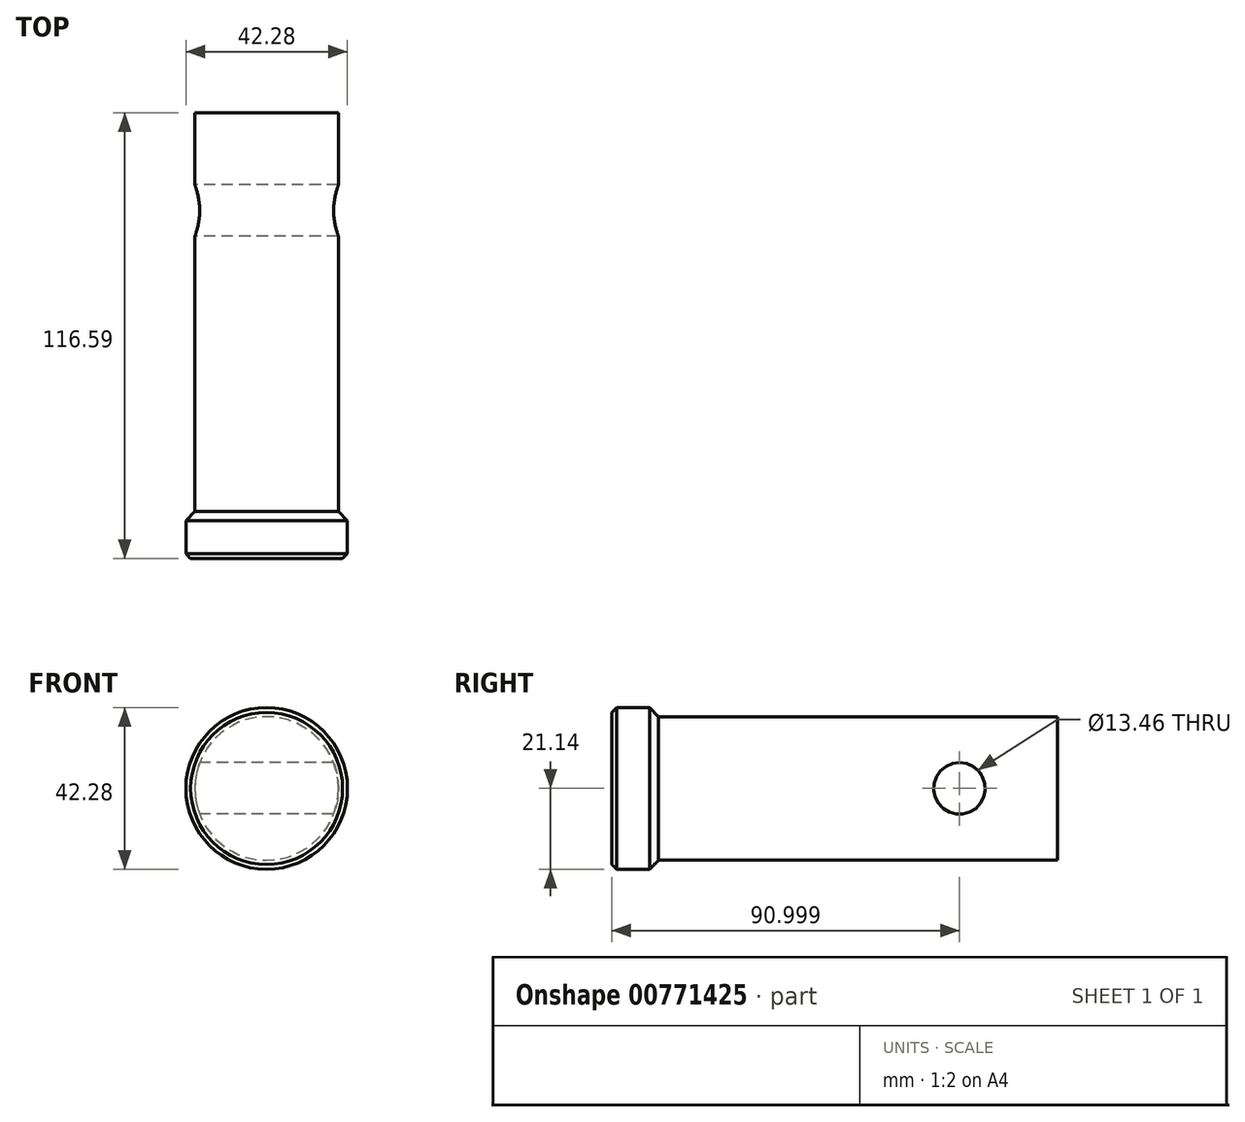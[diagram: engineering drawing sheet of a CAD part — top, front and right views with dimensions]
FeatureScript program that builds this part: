
annotation { "Feature Type Name" : "Feature", "Feature Type Description" : "" }
export const myFeature = defineFeature(function(context is Context, id is Id, definition is map)
    precondition{}
    {
        {
            var Q0;
            Q0=qCreatedBy(makeId("Front.planeOp"),FACE);
            var sketch = newSketch(context, id + "F0", { "sketchPlane" : qUnion([Q0])});
            skCircle(sketch, "E0", {"center": v(0, 0) * mm, "radius": 18.77 * mm});
            skSolve(sketch);
        }
        {
            var Q0;
            Q0 = qSketchRegion(id + "F0", true);
            extrude(context, id + "F1", {"entities" : qUnion([Q0]), "oppositeDirection" : true, "depth" : 101.6 * mm, "offsetDistance" : 25.4 * mm});
        }
        {
            var Q0;
            Q0=qCreatedBy(makeId("Front.planeOp"),FACE);
            var sketch = newSketch(context, id + "F2", { "sketchPlane" : qUnion([Q0])});
            skCircle(sketch, "E1", {"center": v(0, 0) * mm, "radius": 21.14 * mm});
            skSolve(sketch);
        }
        {
            var Q0;
            Q0 = qSketchRegion(id + "F2", true);
            extrude(context, id + "F3", {"entities" : qUnion([Q0]), "operationType" : NewBodyOperationType.ADD, "depth" : 15 * mm, "offsetDistance" : 25.4 * mm});
        }
        {
            var Q0;
            Q0=makeQuery(id+"F3.opExtrude","CAP_EDGE",EDGE,{"disambiguationData":[OSD([sQuery(id+"F2.wireOp",EDGE,"E1")])],"isStart":true});
            chamfer(context, id + "F4", {"entities" : qUnion([Q0]), "width" : 5.08 * mm, "tangentPropagation" : true});
        }
        {
            var Q0;
            Q0=makeQuery(id+"F3.opExtrude","CAP_FACE",FACE,{"disambiguationData":[OSD([sQuery(id+"F2.wireOp",EDGE,"E1")])],"isStart":false});
            chamfer(context, id + "F5", {"entities" : qUnion([Q0]), "chamferType" : ChamferType.OFFSET_ANGLE, "width" : 1.27 * mm, "oppositeDirection" : false, "angle" : 45 * degree, "tangentPropagation" : true});
        }
        {
            var Q0;
            Q0=qCreatedBy(makeId("Right.planeOp"),FACE);
            var sketch = newSketch(context, id + "F6", { "sketchPlane" : qUnion([Q0])});
            skCircle(sketch, "E2", {"center": v(76, 0) * mm, "radius": 6.73 * mm});
            skSolve(sketch);
        }
        {
            var Q0;
            Q0 = qSketchRegion(id + "F6", true);
            extrude(context, id + "F7", {"entities" : qUnion([Q0]), "operationType" : NewBodyOperationType.REMOVE, "depth" : 47.5 * mm, "offsetDistance" : 25.4 * mm, "hasSecondDirection" : true, "secondDirectionOppositeDirection" : true, "secondDirectionDepth" : 25.4 * mm});
        }
    });
